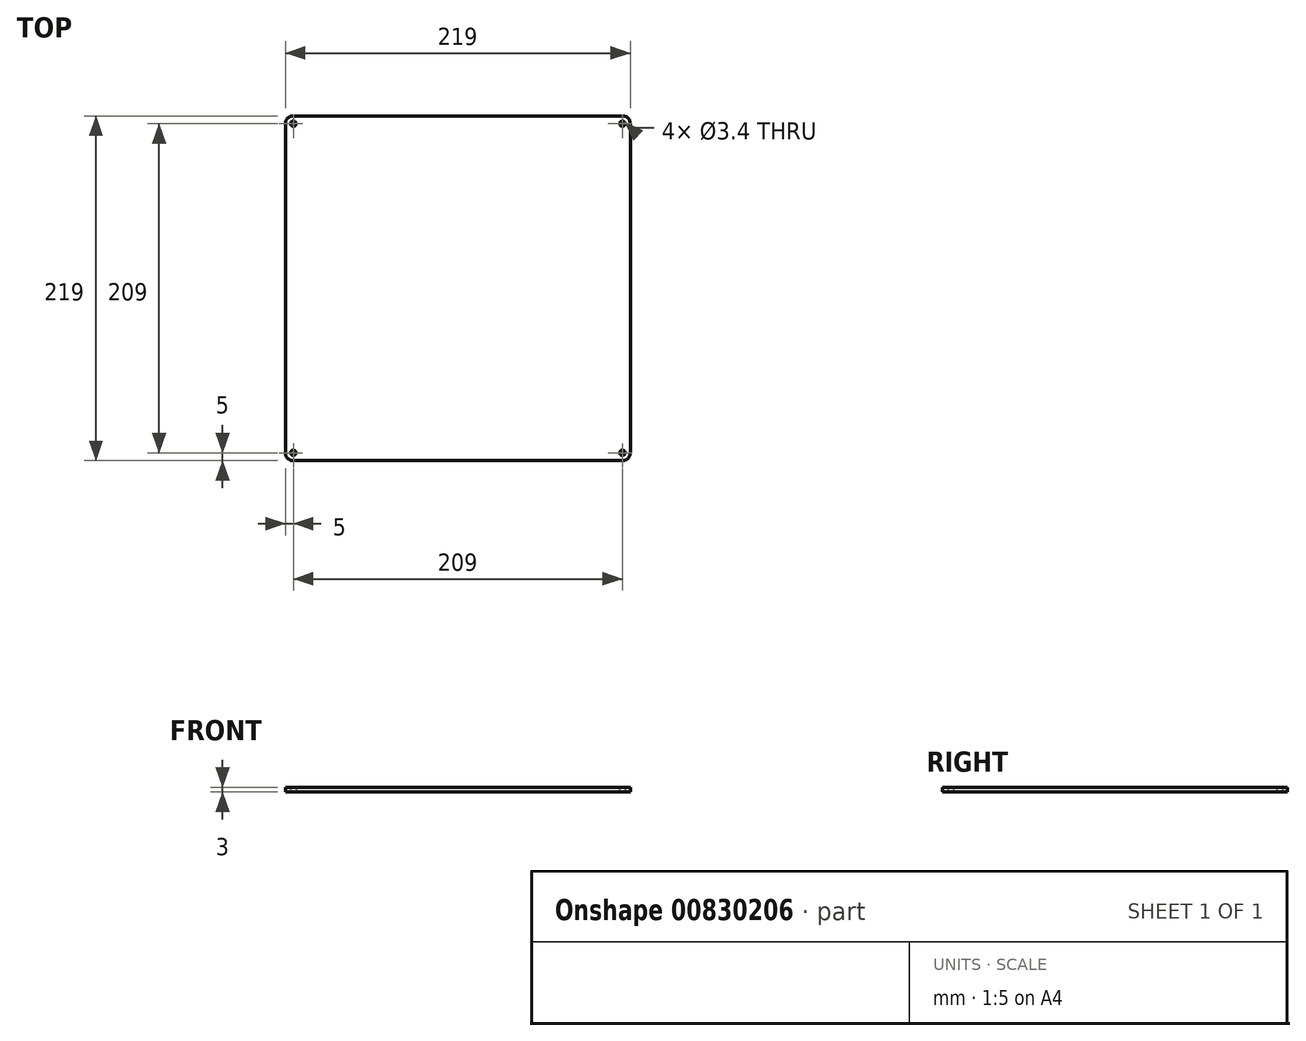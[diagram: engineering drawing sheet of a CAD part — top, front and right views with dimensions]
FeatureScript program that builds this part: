
annotation { "Feature Type Name" : "Feature", "Feature Type Description" : "" }
export const myFeature = defineFeature(function(context is Context, id is Id, definition is map)
    precondition{}
    {
        {
            var Q0;
            Q0=qCreatedBy(makeId("Top.planeOp"),FACE);
            var sketch = newSketch(context, id + "F0", { "sketchPlane" : qUnion([Q0])});
            skLineSegment(sketch, "E0", {"start": v(0, 138.98) * mm, "end": v(0, -196.3) * mm, "construction": true});
            skLineSegment(sketch, "E1", {"start": v(-162.61, 0) * mm, "end": v(192.69, 0) * mm, "construction": true});
            skLineSegment(sketch, "E2.bottom", {"start": v(-104.5, -109.5) * mm, "end": v(104.5, -109.5) * mm});
            skLineSegment(sketch, "E2.top", {"start": v(-104.5, 109.5) * mm, "end": v(104.5, 109.5) * mm});
            skLineSegment(sketch, "E2.left", {"start": v(-109.5, -104.5) * mm, "end": v(-109.5, 104.5) * mm});
            skLineSegment(sketch, "E2.right", {"start": v(109.5, -104.5) * mm, "end": v(109.5, 104.5) * mm});
            skPoint(sketch, "E3.visualSharp", {"position": v(-109.5, -109.5) * mm});
            skArc(sketch, "E3.filletArc", {"start": v(-109.5, -104.5) * mm, "mid": v(-108.04, -108.04) * mm, "end": v(-104.5, -109.5) * mm});
            skPoint(sketch, "E4.visualSharp", {"position": v(109.5, -109.5) * mm});
            skArc(sketch, "E4.filletArc", {"start": v(104.5, -109.5) * mm, "mid": v(108.04, -108.04) * mm, "end": v(109.5, -104.5) * mm});
            skPoint(sketch, "E5.visualSharp", {"position": v(109.5, 109.5) * mm});
            skArc(sketch, "E5.filletArc", {"start": v(109.5, 104.5) * mm, "mid": v(108.04, 108.04) * mm, "end": v(104.5, 109.5) * mm});
            skPoint(sketch, "E6.visualSharp", {"position": v(-109.5, 109.5) * mm});
            skArc(sketch, "E6.filletArc", {"start": v(-104.5, 109.5) * mm, "mid": v(-108.04, 108.04) * mm, "end": v(-109.5, 104.5) * mm});
            skCircle(sketch, "E7", {"center": v(-104.5, 104.5) * mm, "radius": 1.7 * mm});
            skCircle(sketch, "E8.MirrorC", {"center": v(104.5, 104.5) * mm, "radius": 1.7 * mm});
            skCircle(sketch, "E9.MirrorC", {"center": v(-104.5, -104.5) * mm, "radius": 1.7 * mm});
            skCircle(sketch, "E10.MirrorC", {"center": v(104.5, -104.5) * mm, "radius": 1.7 * mm});
            skSolve(sketch);
        }
        {
            var Q0;
            Q0=qSketchRegion(id+"F0",true);
            extrude(context, id + "F1", {"entities" : qUnion([Q0]), "depth" : 3 * mm, "offsetDistance" : 25 * mm});
        }
    });
